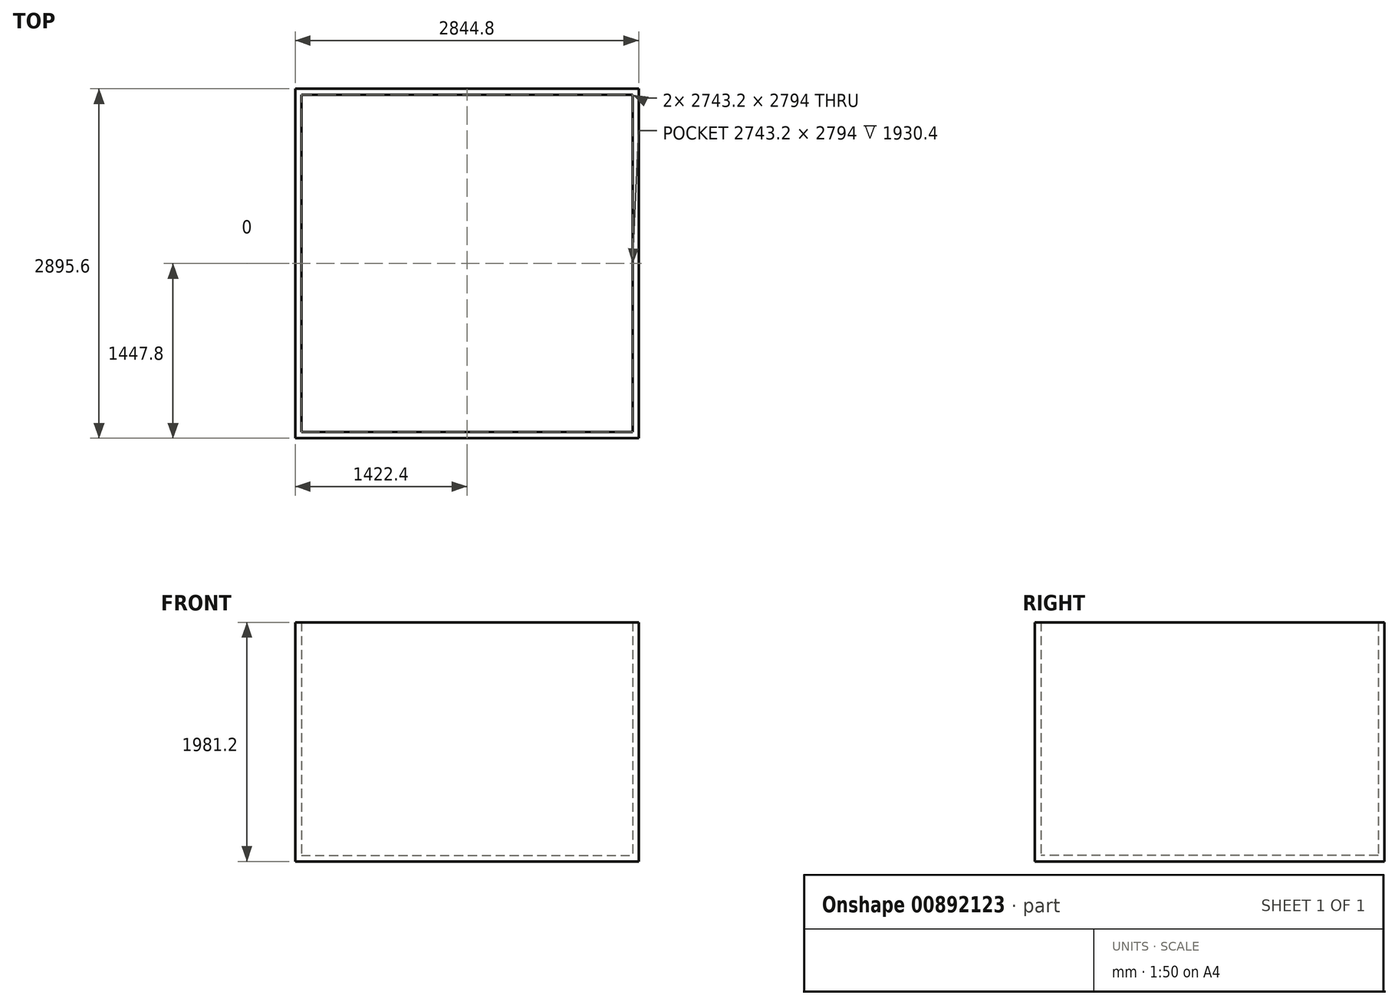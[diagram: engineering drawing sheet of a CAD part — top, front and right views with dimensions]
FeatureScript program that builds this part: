
annotation { "Feature Type Name" : "Feature", "Feature Type Description" : "" }
export const myFeature = defineFeature(function(context is Context, id is Id, definition is map)
    precondition{}
    {
        {
            var Q0;
            Q0=qCreatedBy(makeId("Top.planeOp"),FACE);
            var sketch = newSketch(context, id + "F0", { "sketchPlane" : qUnion([Q0])});
            skLineSegment(sketch, "E0.bottom", {"start": v(-1422.4, 1447.8) * mm, "end": v(1422.4, 1447.8) * mm});
            skLineSegment(sketch, "E0.top", {"start": v(-1422.4, -1447.8) * mm, "end": v(1422.4, -1447.8) * mm});
            skLineSegment(sketch, "E0.left", {"start": v(-1422.4, 1447.8) * mm, "end": v(-1422.4, -1447.8) * mm});
            skLineSegment(sketch, "E0.right", {"start": v(1422.4, 1447.8) * mm, "end": v(1422.4, -1447.8) * mm});
            skPoint(sketch, "E0.middle", {"position": v(0, 0) * mm});
            skSolve(sketch);
        }
        {
            var Q0;
            Q0 = qSketchRegion(id + "F0", true);
            extrude(context, id + "F1", {"entities" : qUnion([Q0]), "endBound" : BoundingType.SYMMETRIC, "depth" : 1981.2 * mm, "offsetDistance" : 25.4 * mm});
        }
        {
            var Q0;
            Q0=makeQuery(id+"F1.opExtrude","CAP_FACE",FACE,{"disambiguationData":[OSD([sQuery(id+"F0.wireOp",EDGE,"E0.bottom"),sQuery(id+"F0.wireOp",EDGE,"E0.top"),sQuery(id+"F0.wireOp",EDGE,"E0.left"),sQuery(id+"F0.wireOp",EDGE,"E0.right")])],"isStart":false});
            shell(context, id + "F2", {"entities" : qUnion([Q0]), "thickness" : 50.8 * mm});
        }
    });
